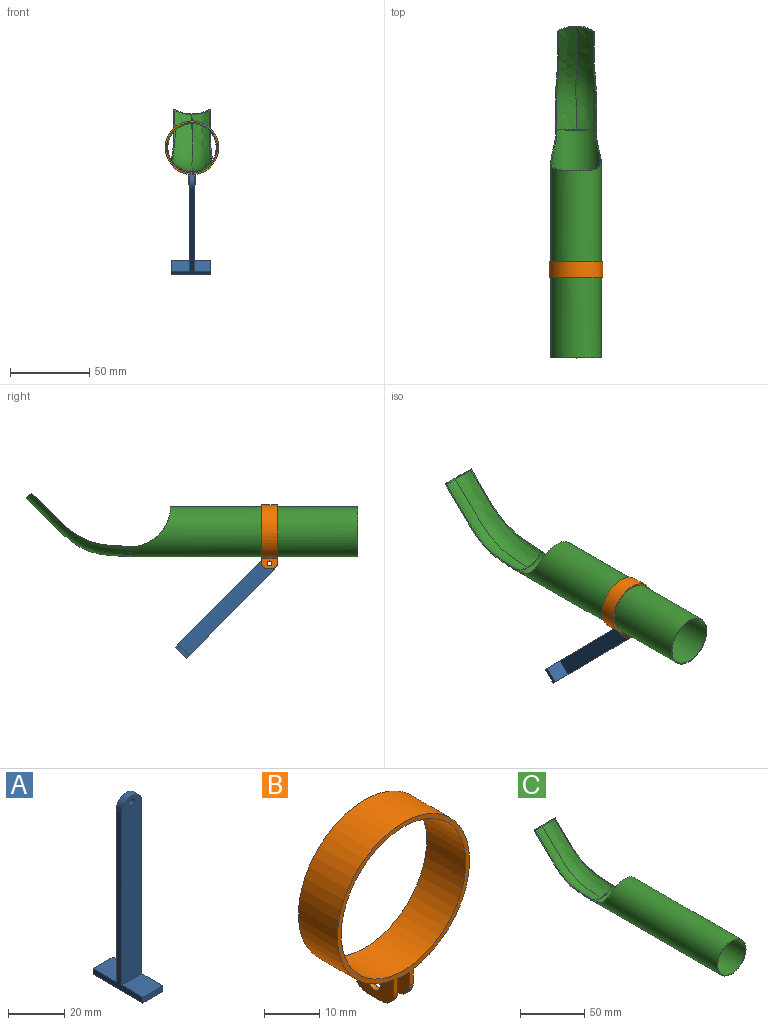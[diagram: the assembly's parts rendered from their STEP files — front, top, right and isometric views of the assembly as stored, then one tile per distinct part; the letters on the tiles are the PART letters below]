
ASSEMBLY  parts=3 mates=2
PART A: 11 faces, bbox 10x25x82.5 mm
  f0: plane 77.5x25mm, normal (1,0,0), area 280mm2, adj f2,f3,f4,f6,f7,f8,f9,f10
  f1: plane 77.5x25mm, normal (-1,0,0), area 280mm2, adj f2,f3,f4,f6,f7,f8,f9,f10
  f2: plane 80x10mm, normal (0,-1,0), area 782.2mm2, adj f0,f1,f4,f5,f6
  f3: plane 80x10mm, normal (0,1,0), area 782.2mm2, adj f0,f1,f4,f5,f10
  f4: cylinder r=5mm len=10mm, axis (0,-1,0), area 45.6mm2, adj f0,f1,f2,f3
  f5: cylinder r=1.5mm len=3mm, axis (0,1,0), area 27.3mm2, adj f2,f3
  f6: plane 10.55x10mm, normal (0,0,1), area 105.5mm2, adj f0,f1,f2,f7
  f7: plane 10x2.5mm, normal (0,-1,0), area 25mm2, adj f0,f1,f6,f9
  f8: plane 10x2.5mm, normal (0,1,0), area 25mm2, adj f0,f1,f9,f10
  f9: plane 25x10mm, normal (0,0,-1), area 250mm2, adj f0,f1,f7,f8
  f10: plane 11.55x10mm, normal (0,0,1), area 115.5mm2, adj f0,f1,f3,f8
PART B: 17 faces, bbox 34x10x40.1 mm
  f0: plane 4x1mm, normal (0,0,-1), area 4mm2, adj f3,f4,f8,f15
  f1: plane 37.11x34mm, normal (0,-1,0), area 110.5mm2, adj f3,f5,f6,f8,f9,f12,f14,f15
  f2: cylinder r=1.5mm len=3mm, axis (1,0,0), area 9.4mm2, adj f8,f15
  f3: cylinder r=3mm len=3mm, axis (-1,0,0), area 4.7mm2, adj f0,f1,f8,f15
  f4: cylinder r=3mm len=3mm, axis (1,0,0), area 4.7mm2, adj f0,f7,f8,f15
  f5: cylinder r=16mm len=32mm, axis (0,1,0), area 1005.3mm2, adj f1,f7
  f6: cylinder r=17mm len=34mm, axis (0,1,0), area 1018mm2, adj f1,f7,f8,f9
  f7: plane 37.11x34mm, normal (0,1,0), area 110.5mm2, adj f4,f5,f6,f8,f9,f13,f14,f15
  f8: plane 10x6.29mm, normal (1,0,0), area 52mm2, adj f0,f1,f2,f3,f4,f6,f7
  f9: plane 10x6.29mm, normal (-1,0,0), area 52mm2, adj f1,f6,f7,f10,f11,f12,f13
  f10: plane 4x1mm, normal (0,0,-1), area 4mm2, adj f9,f12,f13,f14
  f11: cylinder r=1.5mm len=3mm, axis (1,0,0), area 9.4mm2, adj f9,f14
  f12: cylinder r=3mm len=3mm, axis (-1,0,0), area 4.7mm2, adj f1,f9,f10,f14
  f13: cylinder r=3mm len=3mm, axis (1,0,0), area 4.7mm2, adj f7,f9,f10,f14
  f14: plane 10x6mm, normal (1,0,0), area 49.1mm2, adj f1,f7,f10,f11,f12,f13,f16
  f15: plane 10x6mm, normal (-1,0,0), area 49.1mm2, adj f0,f1,f2,f3,f4,f7,f16
  f16: plane 10x3mm, normal (0,0,-1), area 30mm2, adj f1,f7,f14,f15
PART C: 23 faces, bbox 33.2x213.4x53.5 mm
  f0: extruded ~62.52x33.69mm, area 58.3mm2, adj f2,f7,f11,f12,f13,f15,f17,f22
  f1: plane 5.67x2.34mm, normal (0,-0.71,-0.71), area 0.4mm2, adj f6,f16,f22
  f2: plane 5.67x2.34mm, normal (0,-0.71,-0.71), area 0.4mm2, adj f0,f15,f22
  f3: plane 6.8x5.3mm, normal (0,-1,0), area 1.3mm2, adj f6,f7,f8,f10,f14
  f4: plane 13.3x1.52mm, normal (0,-1,0), area 1.4mm2, adj f7,f18,f19
  f5: plane 5.74x4.48mm, normal (0,1,0), area 1mm2, adj f6,f7,f16
  f6: extruded ~62.52x33.69mm, area 58.9mm2, adj f1,f3,f5,f7,f11,f14,f16,f22
  f7: cylinder r=15.3mm len=144.6mm, axis (0,1,0), area 12412.6mm2, adj f0,f3,f4,f5,f6,f9,f10,f12
  f8: cylinder r=15.9mm len=144mm, axis (0,1,0), area 12887.7mm2, adj f3,f9,f10,f12,f13,f14
  f9: plane 31.8x31.8mm, normal (0,-1,0), area 58.8mm2, adj f7,f8
  f10: cylinder r=25.47mm len=31.8mm, axis (1,0,0), area 61.8mm2, adj f3,f7,f8,f12
  f11: plane 23.62x3.64mm, normal (0,0.71,0.71), area 15.6mm2, adj f0,f6,f13,f14,f22
  f12: plane 6.8x5.3mm, normal (0,-1,0), area 1.3mm2, adj f0,f7,f8,f10,f13
  f13: bspline ~71.95x52.29mm, area 1064.2mm2, adj f0,f8,f11,f12,f14
  f14: bspline ~71.94x52.29mm, area 1064.5mm2, adj f3,f6,f8,f11,f13
  f15: offset ~70.14x53.35mm, area 965.8mm2, adj f0,f2,f16,f17,f19,f20
  f16: offset ~70.15x53.36mm, area 965.8mm2, adj f1,f5,f6,f15,f18,f21
  f17: plane 5.74x4.48mm, normal (0,1,0), area 1mm2, adj f0,f7,f15
  f18: extruded ~6.65x1.41mm, area 4.1mm2, adj f4,f7,f16,f19
  f19: extruded ~6.65x1.41mm, area 4.1mm2, adj f4,f7,f15,f18
  f20: plane 5.33x0.74mm, normal (0,0.71,0.71), area 0.1mm2, adj f15,f22
  f21: plane 5.34x0.76mm, normal (0,0.71,0.71), area 0.1mm2, adj f16,f22
  f22: cylinder r=15.97mm len=21.33mm, axis (0,-0.71,-0.71), area 14mm2, adj f0,f1,f2,f6,f11,f20,f21
PLACE A rot(axis=(0.36,-0.36,0.86),98.3deg) t=(25.55,-53.62,-40.49)mm
PLACE B t=(27.05,-74.84,6)mm
PLACE C t=(27.05,8.22,6)mm fixed
MATE slider B.f5 <-> C.f7  axis (0,-1,0) through (27.05,-84.84,6)mm
MATE revolute B.f2 <-> A.f5  axis (-1,0,0) through (24.55,-79.84,-13.96)mm
